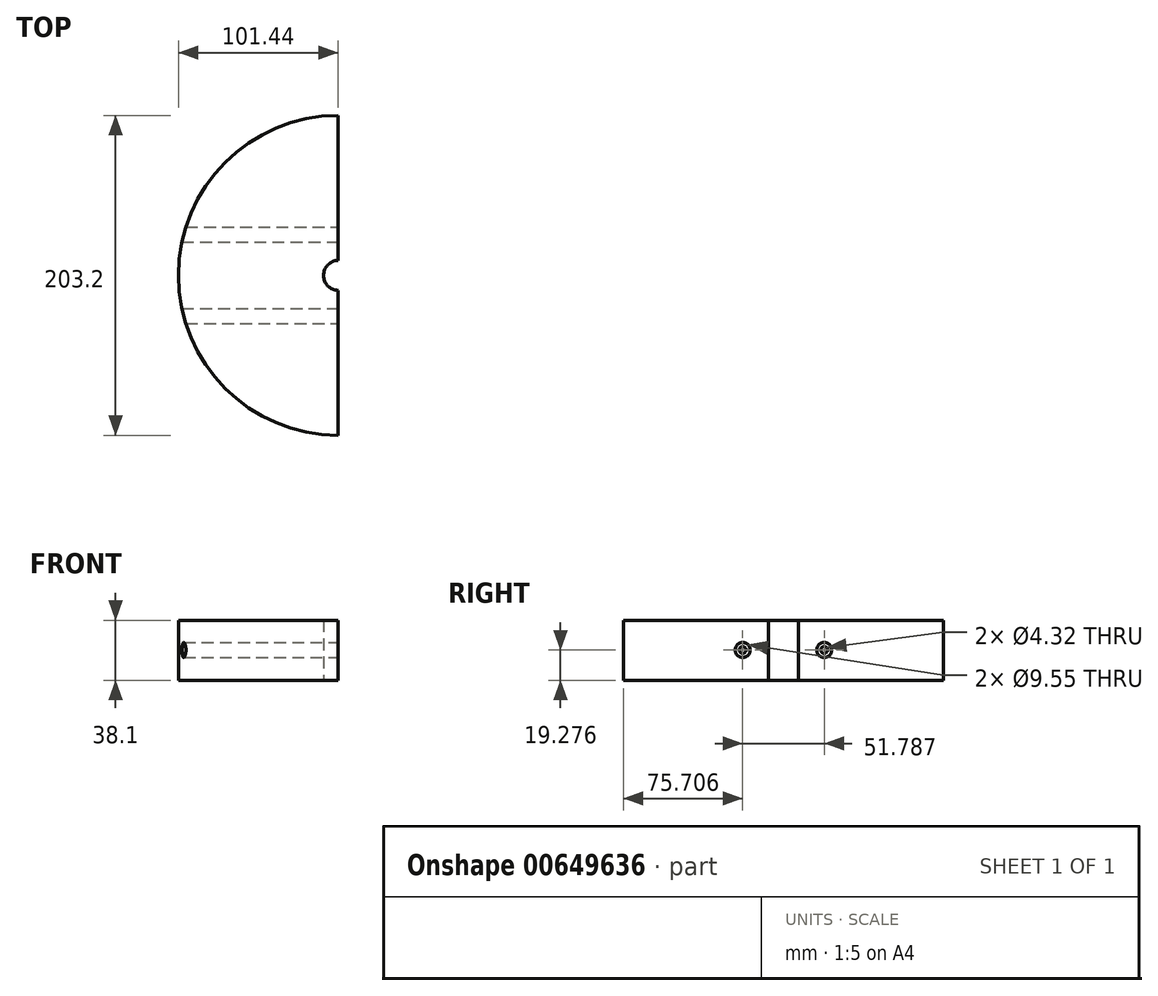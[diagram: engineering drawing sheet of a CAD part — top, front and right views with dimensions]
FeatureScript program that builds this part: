
annotation { "Feature Type Name" : "Feature", "Feature Type Description" : "" }
export const myFeature = defineFeature(function(context is Context, id is Id, definition is map)
    precondition{}
    {
        {
            var Q0;
            Q0=qCreatedBy(makeId("Top.planeOp"),FACE);
            var sketch = newSketch(context, id + "F0", { "sketchPlane" : qUnion([Q0])});
            skLineSegment(sketch, "E0", {"start": v(0, 101.6) * mm, "end": v(0, -101.6) * mm});
            skArc(sketch, "E1", {"start": v(0, 101.6) * mm, "mid": v(-101.4, 0) * mm, "end": v(0, -101.6) * mm});
            skLineSegment(sketch, "E2", {"start": v(0, 9.52) * mm, "end": v(0, -9.52) * mm});
            skArc(sketch, "E3", {"start": v(0, 9.52) * mm, "mid": v(-9.25, 0) * mm, "end": v(0, -9.52) * mm});
            skSolve(sketch);
        }
        {
            var Q0;
            {var subQ0=sQuery(id+"F0.wireOp",EDGE,"E1");Q0=makeQuery(id+"F0.imprint","IMPRINT",FACE,{"disambiguationData":[TD([[makeQuery(id+"F0.imprint","IMPRINT",EDGE,{"derivedFrom":subQ0}),1.0]])]});}
            extrude(context, id + "F1", {"entities" : qUnion([Q0]), "depth" : 38.1 * mm, "offsetDistance" : 25.4 * mm});
        }
        {
            var Q0;
            {var subQ0=sQuery(id+"F0.wireOp",EDGE,"E0");Q0=makeQuery(id+"F1.opExtrude","SWEPT_FACE",FACE,{"disambiguationData":[OSD([subQ0]),TDD([makeQuery(id+"F0.imprint","IMPRINT",EDGE,{"disambiguationData":[TD([[makeQuery(id+"F0.imprint","INTERSECT",VERTEX,{"disambiguationData":[OD(1.0)],"derivedFrom":[subQ0,sQuery(id+"F0.wireOp",EDGE,"E1")]}),1.0]])],"derivedFrom":subQ0})])]});}
            var sketch = newSketch(context, id + "F2", { "sketchPlane" : qUnion([Q0])});
            skCircle(sketch, "E4", {"center": v(-25.9, 19.28) * mm, "radius": 4.76 * mm});
            skCircle(sketch, "E5.MirrorC", {"center": v(25.9, 19.28) * mm, "radius": 4.76 * mm});
            skLineSegment(sketch, "E6", {"start": v(-25.9, 19.28) * mm, "end": v(-25.9, 38.1) * mm});
            skLineSegment(sketch, "E7", {"start": v(-25.9, 38.1) * mm, "end": v(-25.9, 0) * mm});
            skPoint(sketch, "E7.endSnap0", {"position": v(-25.9, 28.69) * mm});
            skLineSegment(sketch, "E8", {"start": v(-101.6, 19.05) * mm, "end": v(-9.52, 19.05) * mm});
            skLineSegment(sketch, "E9", {"start": v(-9.52, 19.05) * mm, "end": v(-25.9, 19.28) * mm});
            skSolve(sketch);
        }
        {
            var Q0;
            Q0=sQuery(id+"F2.wireOp",VERTEX,"E4.center");
            var Q1;
            Q1=makeQuery(id+"F1.opExtrude","SWEPT_BODY",BODY,{"disambiguationData":[OSD([sQuery(id+"F0.wireOp",EDGE,"E0"),sQuery(id+"F0.wireOp",EDGE,"E1"),sQuery(id+"F0.wireOp",EDGE,"E3")])]});
            hole(context, id + "F3", {"style" : HoleStyle.SIMPLE, "endStyle" : HoleEndStyle.THROUGH, "holeDiameter" : 9.55 * mm, "majorDiameter" : 6.35 * mm, "isTappedThrough" : true, "tappedDepth" : 12.7 * mm, "tapClearance" : 3, "locations" : qUnion([Q0]), "scope" : qUnion([Q1])});
        }
        {
            var Q0;
            Q0=sQuery(id+"F2.wireOp",VERTEX,"E5.MirrorC.center");
            var Q1;
            Q1=makeQuery(id+"F1.opExtrude","SWEPT_BODY",BODY,{"disambiguationData":[OSD([sQuery(id+"F0.wireOp",EDGE,"E0"),sQuery(id+"F0.wireOp",EDGE,"E1"),sQuery(id+"F0.wireOp",EDGE,"E3")])]});
            hole(context, id + "F4", {"style" : HoleStyle.SIMPLE, "endStyle" : HoleEndStyle.THROUGH, "holeDiameter" : 9.55 * mm, "majorDiameter" : 6.35 * mm, "isTappedThrough" : true, "tappedDepth" : 12.7 * mm, "tapClearance" : 3, "locations" : qUnion([Q0]), "scope" : qUnion([Q1])});
        }
        {
            var Q0;
            {var subQ0=sQuery(id+"F0.wireOp",EDGE,"E0");Q0=makeQuery(id+"F1.opExtrude","SWEPT_FACE",FACE,{"disambiguationData":[OSD([subQ0]),TDD([makeQuery(id+"F0.imprint","IMPRINT",EDGE,{"disambiguationData":[TD([[makeQuery(id+"F0.imprint","INTERSECT",VERTEX,{"disambiguationData":[OD(1.0)],"derivedFrom":[subQ0,sQuery(id+"F0.wireOp",EDGE,"E1")]}),1.0]])],"derivedFrom":subQ0})])]});}
            var sketch = newSketch(context, id + "F5", { "sketchPlane" : qUnion([Q0])});
            skCircle(sketch, "E10", {"center": v(-25.9, 19.28) * mm, "radius": 2.16 * mm});
            skSolve(sketch);
        }
        {
            var Q0;
            Q0=makeQuery(id+"F5.imprint","IMPRINT",FACE,{"disambiguationData":[TD([[makeQuery(id+"F5.imprint","IMPRINT",EDGE,{"derivedFrom":sQuery(id+"F5.wireOp",EDGE,"E10")}),-1.0]])]});
            extrude(context, id + "F6", {"entities" : qUnion([Q0]), "depth" : 0.03 * mm, "offsetDistance" : 25.4 * mm});
        }
        {
            var Q0;
            Q0=makeQuery(id+"F6.opExtrude","SWEPT_BODY",BODY,{"disambiguationData":[OSD([sQuery(id+"F3.hole-0.sketch.wireOp",EDGE,"core_line_2"),sQuery(id+"F3.hole-0.sketch.wireOp",EDGE,"core_line_3"),sQuery(id+"F5.wireOp",EDGE,"E10")])]});
            var Q1;
            Q1=qCreatedBy(makeId("Front.planeOp"),FACE);
            mirror(context, id + "F7", {"entities" : qUnion([Q0]), "mirrorPlane" : qUnion([Q1])});
        }
    });
